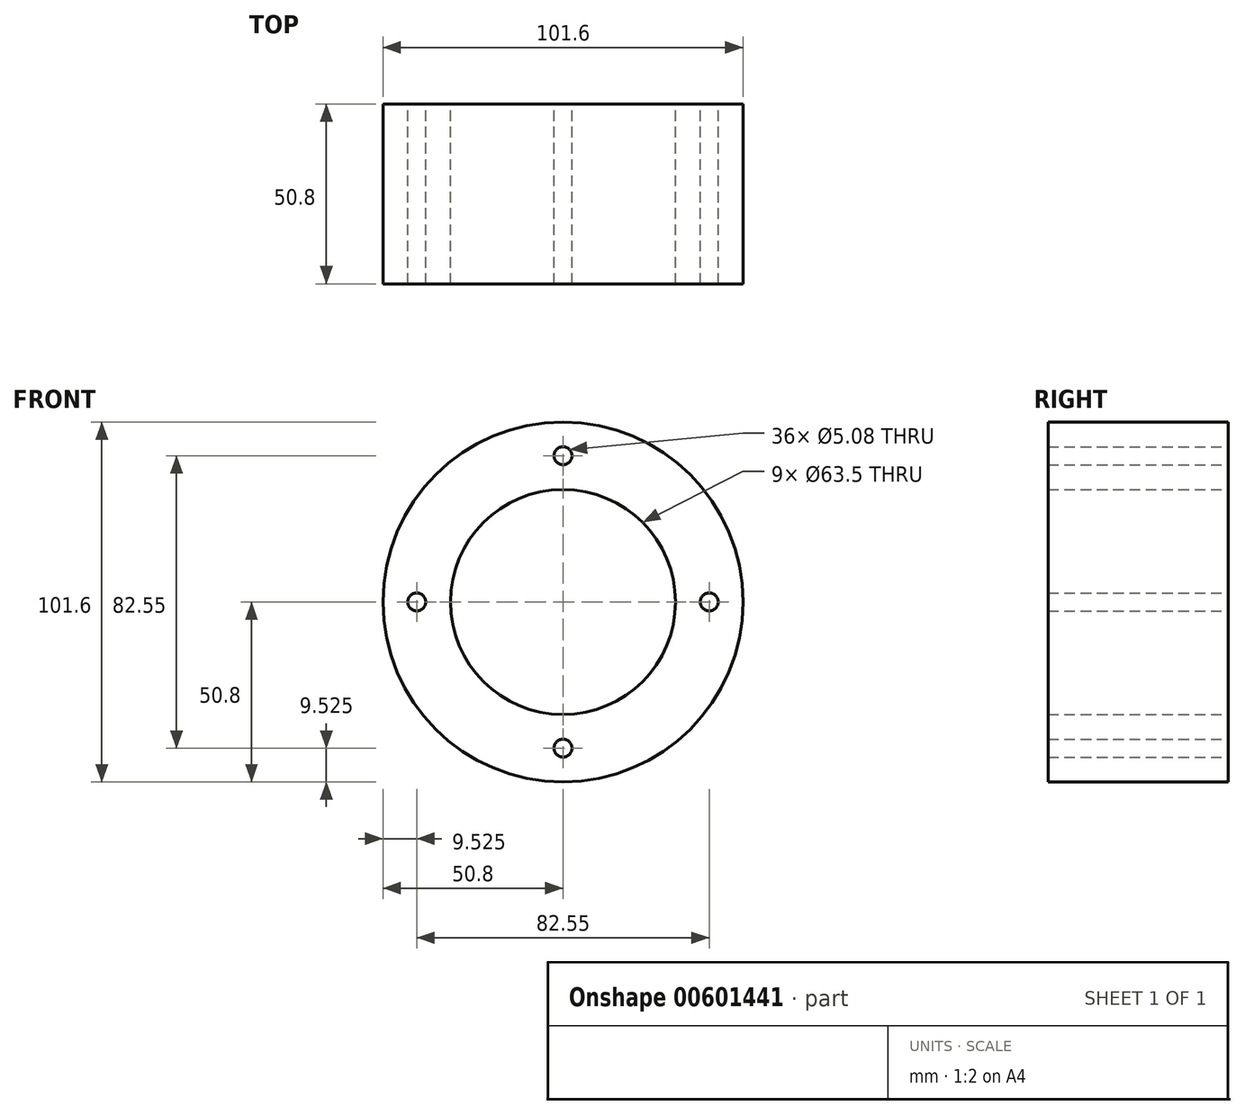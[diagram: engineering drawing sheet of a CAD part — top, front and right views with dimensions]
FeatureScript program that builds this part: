
annotation { "Feature Type Name" : "Feature", "Feature Type Description" : "" }
export const myFeature = defineFeature(function(context is Context, id is Id, definition is map)
    precondition{}
    {
        {
            var Q0;
            Q0=qCreatedBy(makeId("Front.planeOp"),FACE);
            var sketch = newSketch(context, id + "F0", { "sketchPlane" : qUnion([Q0])});
            skCircle(sketch, "E0", {"center": v(0, 0) * mm, "radius": 50.8 * mm});
            skCircle(sketch, "E1", {"center": v(0, 0) * mm, "radius": 31.75 * mm});
            skCircle(sketch, "E2", {"center": v(0, 41.28) * mm, "radius": 2.54 * mm});
            skCircle(sketch, "E3", {"center": v(-41.28, 0) * mm, "radius": 2.54 * mm});
            skCircle(sketch, "E4", {"center": v(0, -41.28) * mm, "radius": 2.54 * mm});
            skCircle(sketch, "E5", {"center": v(41.28, 0) * mm, "radius": 2.54 * mm});
            skSolve(sketch);
        }
        {
            var Q0;
            Q0 = qSketchRegion(id + "F0", true);
            extrude(context, id + "F1", {"entities" : qUnion([Q0]), "endBound" : BoundingType.SYMMETRIC, "depth" : 50.8 * mm, "offsetDistance" : 25.4 * mm});
        }
    });
